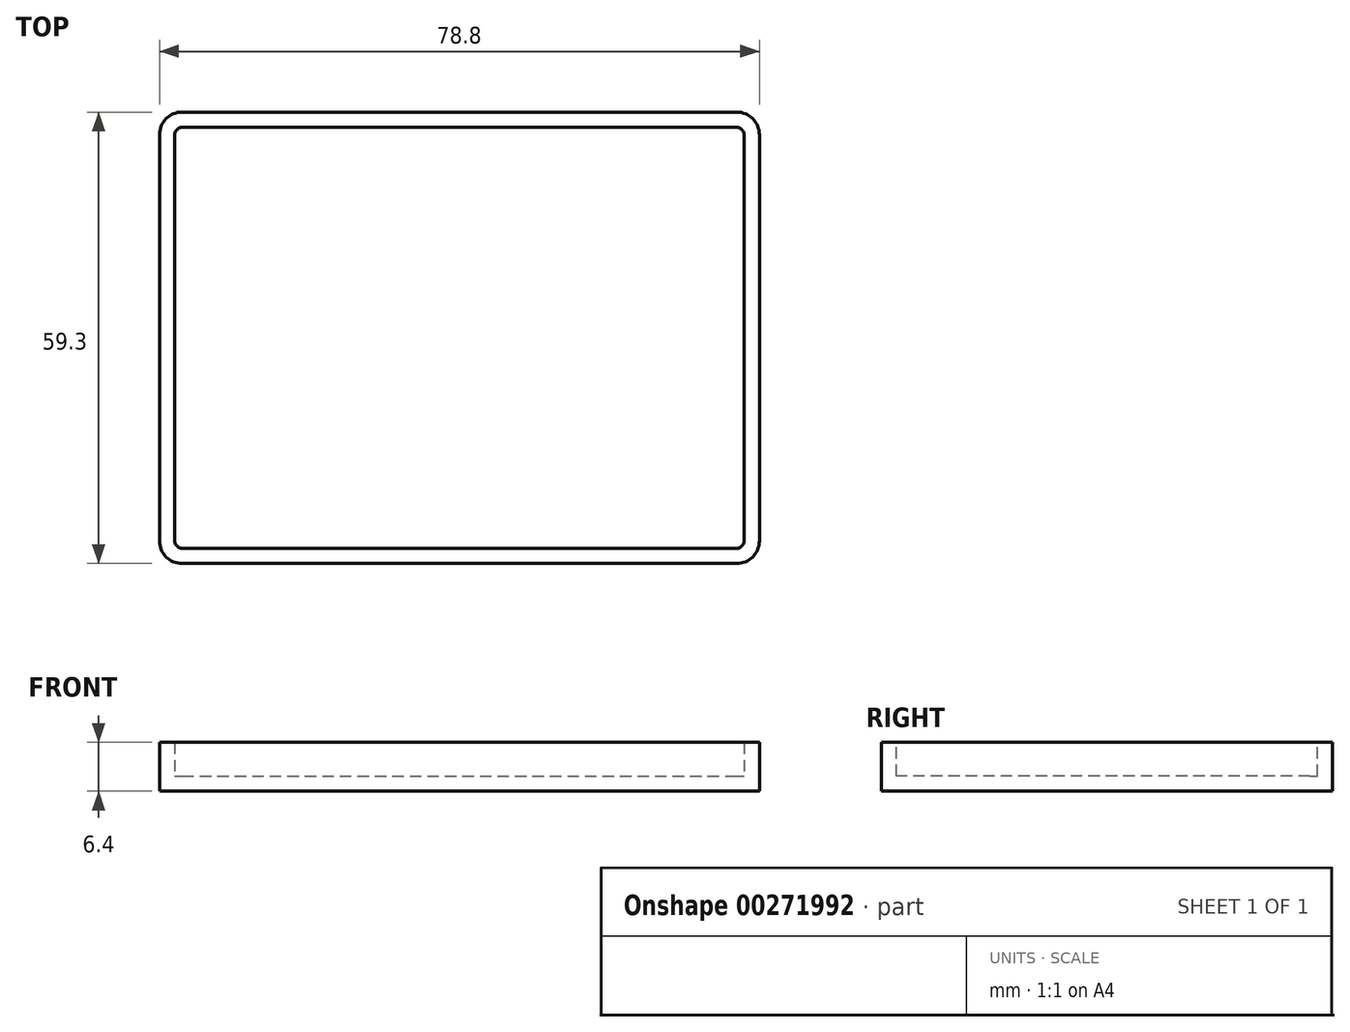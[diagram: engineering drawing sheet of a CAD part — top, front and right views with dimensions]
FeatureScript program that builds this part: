
annotation { "Feature Type Name" : "Feature", "Feature Type Description" : "" }
export const myFeature = defineFeature(function(context is Context, id is Id, definition is map)
    precondition{}
    {
        {
            var Q0;
            Q0=qCreatedBy(makeId("Top.planeOp"),FACE);
            var sketch = newSketch(context, id + "F0", { "sketchPlane" : qUnion([Q0])});
            skLineSegment(sketch, "E0.bottom", {"start": v(-19.31, 12.91) * mm, "end": v(59.49, 12.91) * mm});
            skLineSegment(sketch, "E0.top", {"start": v(-19.31, -46.39) * mm, "end": v(59.49, -46.39) * mm});
            skLineSegment(sketch, "E0.left", {"start": v(-19.31, 12.91) * mm, "end": v(-19.31, -46.39) * mm});
            skLineSegment(sketch, "E0.right", {"start": v(59.49, 12.91) * mm, "end": v(59.49, -46.39) * mm});
            skSolve(sketch);
        }
        {
            var Q0;
            Q0=makeQuery(id+"F0.imprint","IMPRINT",FACE,{"disambiguationData":[TD([[makeQuery(id+"F0.imprint","IMPRINT",EDGE,{"derivedFrom":sQuery(id+"F0.wireOp",EDGE,"E0.bottom")}),-1.0]])]});
            extrude(context, id + "F1", {"entities" : qUnion([Q0]), "depth" : 6.4 * mm});
        }
        {
            var Q0;
            Q0=makeQuery(id+"F1.opExtrude","SWEPT_EDGE",EDGE,{"disambiguationData":[OSD([sQuery(id+"F0.wireOp",EDGE,"E0.top"),sQuery(id+"F0.wireOp",EDGE,"E0.left")])]});
            var Q1;
            Q1=makeQuery(id+"F1.opExtrude","SWEPT_EDGE",EDGE,{"disambiguationData":[OSD([sQuery(id+"F0.wireOp",EDGE,"E0.top"),sQuery(id+"F0.wireOp",EDGE,"E0.right")])]});
            var Q2;
            Q2=makeQuery(id+"F1.opExtrude","SWEPT_EDGE",EDGE,{"disambiguationData":[OSD([sQuery(id+"F0.wireOp",EDGE,"E0.bottom"),sQuery(id+"F0.wireOp",EDGE,"E0.right")])]});
            var Q3;
            Q3=makeQuery(id+"F1.opExtrude","SWEPT_EDGE",EDGE,{"disambiguationData":[OSD([sQuery(id+"F0.wireOp",EDGE,"E0.bottom"),sQuery(id+"F0.wireOp",EDGE,"E0.left")])]});
            fillet(context, id + "F2", {"entities" : qUnion([Q0, Q1, Q2, Q3]), "radius" : 3 * mm, "tangentPropagation" : true, "allowEdgeOverflow" : false});
        }
        {
            var Q0;
            Q0=makeQuery(id+"F1.opExtrude","CAP_FACE",FACE,{"disambiguationData":[OSD([sQuery(id+"F0.wireOp",EDGE,"E0.bottom"),sQuery(id+"F0.wireOp",EDGE,"E0.top"),sQuery(id+"F0.wireOp",EDGE,"E0.left"),sQuery(id+"F0.wireOp",EDGE,"E0.right")])],"isStart":false});
            shell(context, id + "F3", {"entities" : qUnion([Q0]), "thickness" : 2 * mm});
        }
    });
